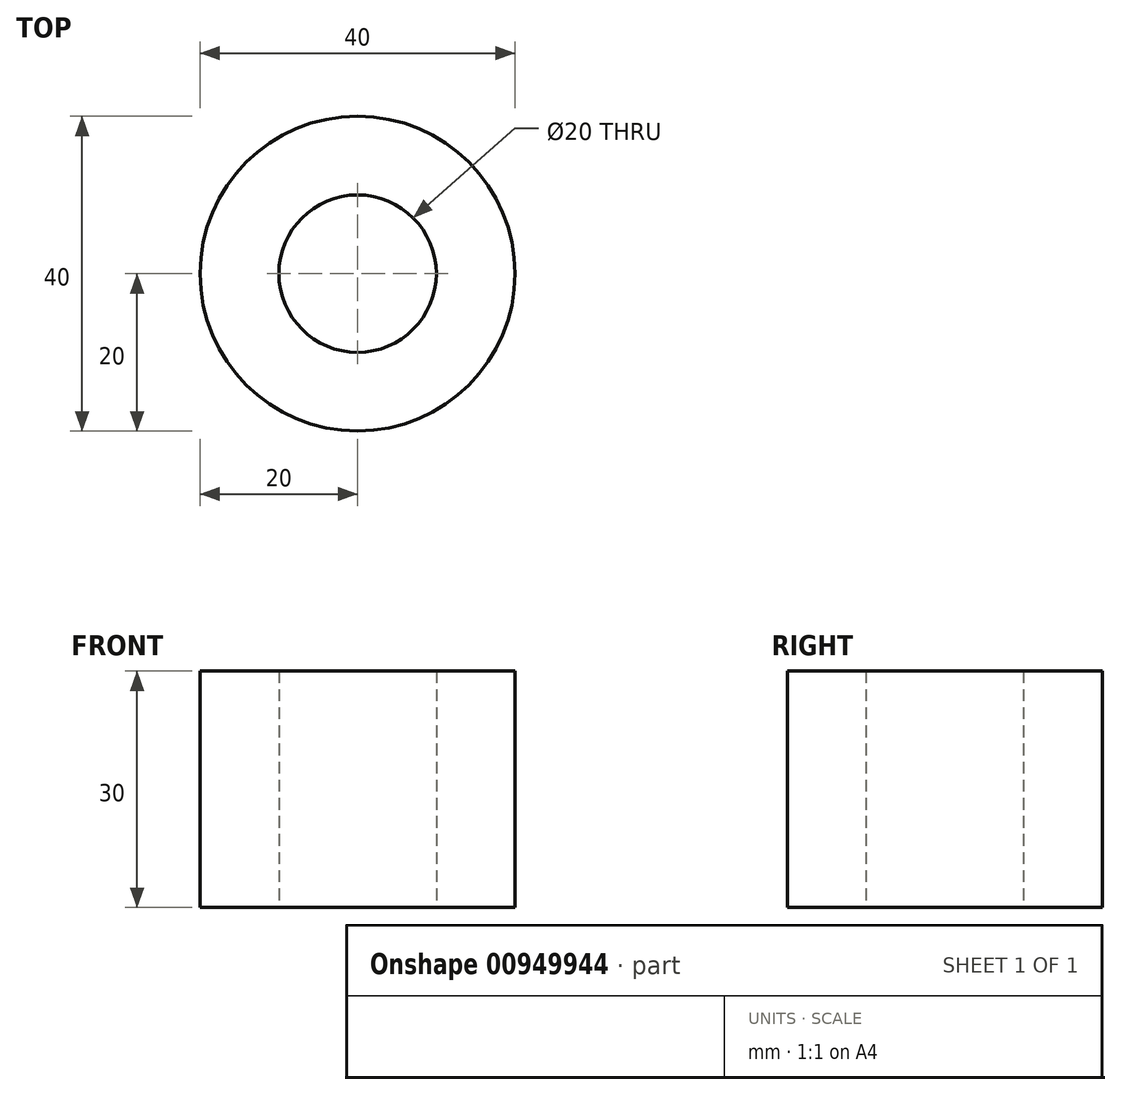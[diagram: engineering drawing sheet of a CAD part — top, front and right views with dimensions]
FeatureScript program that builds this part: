
annotation { "Feature Type Name" : "Feature", "Feature Type Description" : "" }
export const myFeature = defineFeature(function(context is Context, id is Id, definition is map)
    precondition{}
    {
        {
            var Q0;
            Q0=qCreatedBy(makeId("Top.planeOp"),FACE);
            var sketch = newSketch(context, id + "F0", { "sketchPlane" : qUnion([Q0])});
            skCircle(sketch, "E0", {"center": v(0, 0) * mm, "radius": 10 * mm});
            skCircle(sketch, "E1", {"center": v(0, 0) * mm, "radius": 20 * mm});
            skSolve(sketch);
        }
        {
            var Q0;
            Q0=makeQuery(id+"F0.imprint","IMPRINT",FACE,{"disambiguationData":[TD([[makeQuery(id+"F0.imprint","IMPRINT",EDGE,{"derivedFrom":sQuery(id+"F0.wireOp",EDGE,"E0")}),-1.0]])]});
            extrude(context, id + "F1", {"entities" : qUnion([Q0]), "depth" : 30 * mm, "offsetDistance" : 25 * mm});
        }
    });
